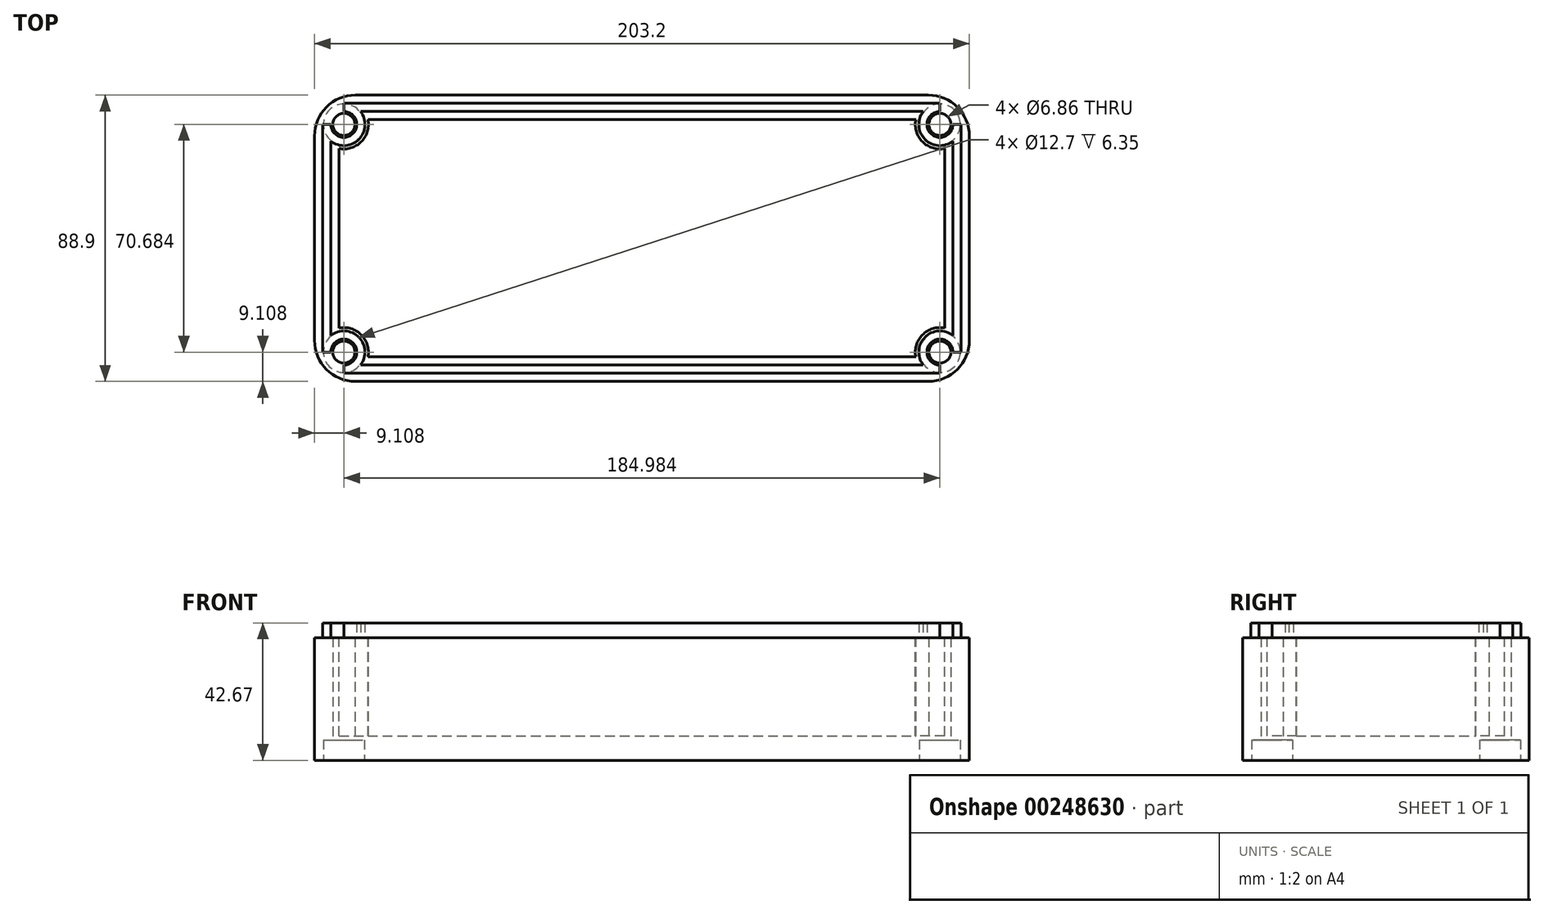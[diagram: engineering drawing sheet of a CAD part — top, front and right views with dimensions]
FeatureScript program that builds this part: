
annotation { "Feature Type Name" : "Feature", "Feature Type Description" : "" }
export const myFeature = defineFeature(function(context is Context, id is Id, definition is map)
    precondition{}
    {
        {
            var Q0;
            Q0=qCreatedBy(makeId("Top.planeOp"),FACE);
            var sketch = newSketch(context, id + "F0", { "sketchPlane" : qUnion([Q0])});
            skLineSegment(sketch, "E0", {"start": v(12.7, 0) * mm, "end": v(190.5, 0) * mm});
            skArc(sketch, "E1", {"start": v(190.5, 0) * mm, "mid": v(199.48, 3.72) * mm, "end": v(203.2, 12.7) * mm});
            skLineSegment(sketch, "E2", {"start": v(203.2, 12.7) * mm, "end": v(203.2, 44.45) * mm});
            skArc(sketch, "E3", {"start": v(0, 12.7) * mm, "mid": v(3.72, 3.72) * mm, "end": v(12.7, 0) * mm});
            skLineSegment(sketch, "E4", {"start": v(0, 12.7) * mm, "end": v(0, 44.45) * mm});
            skLineSegment(sketch, "E5", {"start": v(0, 44.45) * mm, "end": v(203.2, 44.45) * mm, "construction": true});
            skArc(sketch, "E6.MirrorCS", {"start": v(190.5, 88.9) * mm, "mid": v(199.48, 85.18) * mm, "end": v(203.2, 76.2) * mm});
            skArc(sketch, "E7.MirrorCS", {"start": v(0, 76.2) * mm, "mid": v(3.72, 85.18) * mm, "end": v(12.7, 88.9) * mm});
            skLineSegment(sketch, "E8.MirrorCS", {"start": v(12.7, 88.9) * mm, "end": v(190.5, 88.9) * mm});
            skLineSegment(sketch, "E9.MirrorCS", {"start": v(203.2, 76.2) * mm, "end": v(203.2, 44.45) * mm});
            skLineSegment(sketch, "E10.MirrorCS", {"start": v(0, 76.2) * mm, "end": v(0, 44.45) * mm});
            skSolve(sketch);
        }
        {
            var Q0;
            Q0=makeQuery(id+"F0.imprint","IMPRINT",FACE,{"disambiguationData":[TD([[makeQuery(id+"F0.imprint","IMPRINT",EDGE,{"derivedFrom":sQuery(id+"F0.wireOp",EDGE,"E0")}),1.0]])]});
            extrude(context, id + "F1", {"entities" : qUnion([Q0]), "depth" : 38.1 * mm});
        }
        {
            var Q0;
            Q0=makeQuery(id+"F1.opExtrude","CAP_FACE",FACE,{"disambiguationData":[OSD([sQuery(id+"F0.wireOp",EDGE,"E0"),sQuery(id+"F0.wireOp",EDGE,"E1"),sQuery(id+"F0.wireOp",EDGE,"E2"),sQuery(id+"F0.wireOp",EDGE,"E3"),sQuery(id+"F0.wireOp",EDGE,"E4"),sQuery(id+"F0.wireOp",EDGE,"E6.MirrorCS"),sQuery(id+"F0.wireOp",EDGE,"E7.MirrorCS"),sQuery(id+"F0.wireOp",EDGE,"E8.MirrorCS"),sQuery(id+"F0.wireOp",EDGE,"E9.MirrorCS"),sQuery(id+"F0.wireOp",EDGE,"E10.MirrorCS")])],"isStart":false});
            shell(context, id + "F2", {"entities" : qUnion([Q0]), "thickness" : 7.62 * mm});
        }
        {
            var Q0;
            Q0=makeQuery(id+"F1.opExtrude","CAP_FACE",FACE,{"disambiguationData":[OSD([sQuery(id+"F0.wireOp",EDGE,"E0"),sQuery(id+"F0.wireOp",EDGE,"E1"),sQuery(id+"F0.wireOp",EDGE,"E2"),sQuery(id+"F0.wireOp",EDGE,"E3"),sQuery(id+"F0.wireOp",EDGE,"E4"),sQuery(id+"F0.wireOp",EDGE,"E6.MirrorCS"),sQuery(id+"F0.wireOp",EDGE,"E7.MirrorCS"),sQuery(id+"F0.wireOp",EDGE,"E8.MirrorCS"),sQuery(id+"F0.wireOp",EDGE,"E9.MirrorCS"),sQuery(id+"F0.wireOp",EDGE,"E10.MirrorCS")])],"isStart":false});
            var sketch = newSketch(context, id + "F3", { "sketchPlane" : qUnion([Q0])});
            skCircle(sketch, "E11", {"center": v(9.1, 79.8) * mm, "radius": 7.62 * mm});
            skLineSegment(sketch, "E12", {"start": v(101.6, 81.28) * mm, "end": v(101.6, 7.62) * mm, "construction": true});
            skLineSegment(sketch, "E13", {"start": v(7.62, 44.45) * mm, "end": v(195.58, 44.45) * mm, "construction": true});
            skCircle(sketch, "E14.MirrorC", {"center": v(194.1, 79.8) * mm, "radius": 7.62 * mm});
            skCircle(sketch, "E15.MirrorC", {"center": v(9.1, 9.1) * mm, "radius": 7.62 * mm});
            skCircle(sketch, "E16.MirrorC", {"center": v(194.1, 9.1) * mm, "radius": 7.62 * mm});
            skSolve(sketch);
        }
        {
            var Q0;
            Q0 = qSketchRegion(id + "F3", true);
            var Q1;
            Q1=makeQuery(id+"F2.opShell","OFFSET_FACE",FACE,{"disambiguationData":[OSD([sQuery(id+"F0.wireOp",EDGE,"E0"),sQuery(id+"F0.wireOp",EDGE,"E1"),sQuery(id+"F0.wireOp",EDGE,"E2"),sQuery(id+"F0.wireOp",EDGE,"E3"),sQuery(id+"F0.wireOp",EDGE,"E4"),sQuery(id+"F0.wireOp",EDGE,"E6.MirrorCS"),sQuery(id+"F0.wireOp",EDGE,"E7.MirrorCS"),sQuery(id+"F0.wireOp",EDGE,"E8.MirrorCS"),sQuery(id+"F0.wireOp",EDGE,"E9.MirrorCS"),sQuery(id+"F0.wireOp",EDGE,"E10.MirrorCS")])]});
            extrude(context, id + "F4", {"entities" : qUnion([Q0]), "operationType" : NewBodyOperationType.ADD, "endBound" : BoundingType.UP_TO_SURFACE, "oppositeDirection" : true, "endBoundEntityFace" : qUnion([Q1]), "depth" : 25.4 * mm});
        }
        {
            var Q0;
            Q0=makeQuery(id+"F4.boolean.opBoolean","MERGE",FACE,{"derivedFrom":[makeQuery(id+"F1.opExtrude","CAP_FACE",FACE,{"disambiguationData":[OSD([sQuery(id+"F0.wireOp",EDGE,"E0"),sQuery(id+"F0.wireOp",EDGE,"E1"),sQuery(id+"F0.wireOp",EDGE,"E2"),sQuery(id+"F0.wireOp",EDGE,"E3"),sQuery(id+"F0.wireOp",EDGE,"E4"),sQuery(id+"F0.wireOp",EDGE,"E6.MirrorCS"),sQuery(id+"F0.wireOp",EDGE,"E7.MirrorCS"),sQuery(id+"F0.wireOp",EDGE,"E8.MirrorCS"),sQuery(id+"F0.wireOp",EDGE,"E9.MirrorCS"),sQuery(id+"F0.wireOp",EDGE,"E10.MirrorCS")])],"isStart":false}),makeQuery(id+"F4.opExtrude","CAP_FACE",FACE,{"disambiguationData":[OSD([sQuery(id+"F3.wireOp",EDGE,"E14.MirrorC")])],"isStart":true}),makeQuery(id+"F4.opExtrude","CAP_FACE",FACE,{"disambiguationData":[OSD([sQuery(id+"F3.wireOp",EDGE,"E11")])],"isStart":true}),makeQuery(id+"F4.opExtrude","CAP_FACE",FACE,{"disambiguationData":[OSD([sQuery(id+"F3.wireOp",EDGE,"E15.MirrorC")])],"isStart":true}),makeQuery(id+"F4.opExtrude","CAP_FACE",FACE,{"disambiguationData":[OSD([sQuery(id+"F3.wireOp",EDGE,"E16.MirrorC")])],"isStart":true})]});
            var sketch = newSketch(context, id + "F5", { "sketchPlane" : qUnion([Q0])});
            skLineSegment(sketch, "E17.0", {"start": v(101.6, 86.36) * mm, "end": v(194.1, 86.36) * mm});
            skLineSegment(sketch, "E18.0", {"start": v(200.66, 44.45) * mm, "end": v(200.66, 79.8) * mm});
            skLineSegment(sketch, "E19", {"start": v(7.62, 44.45) * mm, "end": v(195.58, 44.45) * mm, "construction": true});
            skLineSegment(sketch, "E20", {"start": v(101.6, 81.28) * mm, "end": v(101.6, 7.62) * mm, "construction": true});
            skLineSegment(sketch, "E21.0", {"start": v(101.6, 83.82) * mm, "end": v(188.9, 83.82) * mm});
            skLineSegment(sketch, "E22.0", {"start": v(198.12, 44.45) * mm, "end": v(198.12, 74.6) * mm});
            skCircle(sketch, "E23", {"center": v(194.1, 79.8) * mm, "radius": 6.57 * mm});
            skCircle(sketch, "E24", {"center": v(194.1, 79.8) * mm, "radius": 4.03 * mm});
            skCircle(sketch, "E25.MirrorC", {"center": v(9.1, 79.8) * mm, "radius": 4.03 * mm});
            skCircle(sketch, "E26.MirrorC", {"center": v(9.1, 79.8) * mm, "radius": 6.57 * mm});
            skLineSegment(sketch, "E27.MirrorCS", {"start": v(5.08, 44.45) * mm, "end": v(5.08, 74.6) * mm});
            skLineSegment(sketch, "E28.MirrorCS", {"start": v(101.6, 83.82) * mm, "end": v(14.3, 83.82) * mm});
            skLineSegment(sketch, "E29.MirrorCS", {"start": v(101.6, 86.36) * mm, "end": v(9.1, 86.36) * mm});
            skLineSegment(sketch, "E30.MirrorCS", {"start": v(2.54, 44.45) * mm, "end": v(2.54, 79.8) * mm});
            skLineSegment(sketch, "E31.MirrorCS", {"start": v(101.6, 5.08) * mm, "end": v(188.9, 5.08) * mm});
            skLineSegment(sketch, "E32.MirrorCS", {"start": v(200.66, 44.45) * mm, "end": v(200.66, 9.1) * mm});
            skLineSegment(sketch, "E33.MirrorCS", {"start": v(101.6, 2.54) * mm, "end": v(194.1, 2.54) * mm});
            skCircle(sketch, "E34.MirrorC", {"center": v(194.1, 9.1) * mm, "radius": 4.03 * mm});
            skCircle(sketch, "E35.MirrorC", {"center": v(194.1, 9.1) * mm, "radius": 6.57 * mm});
            skLineSegment(sketch, "E36.MirrorCS", {"start": v(198.12, 44.45) * mm, "end": v(198.12, 14.3) * mm});
            skCircle(sketch, "E37.MirrorC", {"center": v(9.1, 9.1) * mm, "radius": 4.03 * mm});
            skCircle(sketch, "E38.MirrorC", {"center": v(9.1, 9.1) * mm, "radius": 6.57 * mm});
            skLineSegment(sketch, "E39.MirrorCS", {"start": v(101.6, 5.08) * mm, "end": v(14.3, 5.08) * mm});
            skLineSegment(sketch, "E40.MirrorCS", {"start": v(101.6, 2.54) * mm, "end": v(9.1, 2.54) * mm});
            skLineSegment(sketch, "E41.MirrorCS", {"start": v(5.08, 44.45) * mm, "end": v(5.08, 14.3) * mm});
            skLineSegment(sketch, "E42.MirrorCS", {"start": v(2.54, 44.45) * mm, "end": v(2.54, 9.1) * mm});
            skLineSegment(sketch, "E43", {"start": v(200.66, 79.8) * mm, "end": v(198.12, 79.8) * mm});
            skLineSegment(sketch, "E44", {"start": v(194.1, 86.36) * mm, "end": v(194.1, 83.82) * mm});
            skLineSegment(sketch, "E45.MirrorCS", {"start": v(194.1, 2.54) * mm, "end": v(194.1, 5.08) * mm});
            skLineSegment(sketch, "E46.MirrorCS", {"start": v(200.66, 9.1) * mm, "end": v(198.12, 9.1) * mm});
            skLineSegment(sketch, "E47.MirrorCS", {"start": v(9.1, 86.36) * mm, "end": v(9.1, 83.82) * mm});
            skLineSegment(sketch, "E48.MirrorCS", {"start": v(2.54, 79.8) * mm, "end": v(5.08, 79.8) * mm});
            skLineSegment(sketch, "E49.MirrorCS", {"start": v(2.54, 9.1) * mm, "end": v(5.08, 9.1) * mm});
            skLineSegment(sketch, "E50.MirrorCS", {"start": v(9.1, 2.54) * mm, "end": v(9.1, 5.08) * mm});
            skSolve(sketch);
        }
        {
            var Q0;
            {var subQ4=sQuery(id+"F5.wireOp",EDGE,"E47.MirrorCS");Q0=makeQuery(id+"F5.imprint","IMPRINT",FACE,{"disambiguationData":[TD([[makeQuery(id+"F5.imprint","IMPRINT",EDGE,{"derivedFrom":subQ4}),1.0]])]});}
            var Q1;
            {var subQ5=sQuery(id+"F5.wireOp",EDGE,"E17.0");Q1=makeQuery(id+"F5.imprint","IMPRINT",FACE,{"disambiguationData":[TD([[makeQuery(id+"F5.imprint","IMPRINT",EDGE,{"derivedFrom":subQ5}),-1.0]])]});}
            var Q2;
            {var subQ0=sQuery(id+"F5.wireOp",EDGE,"E43");Q2=makeQuery(id+"F5.imprint","IMPRINT",FACE,{"disambiguationData":[TD([[makeQuery(id+"F5.imprint","IMPRINT",EDGE,{"derivedFrom":subQ0}),1.0]])]});}
            var Q3;
            {var subQ1=sQuery(id+"F5.wireOp",EDGE,"E18.0");Q3=makeQuery(id+"F5.imprint","IMPRINT",FACE,{"disambiguationData":[TD([[makeQuery(id+"F5.imprint","IMPRINT",EDGE,{"derivedFrom":subQ1}),1.0]])]});}
            var Q4;
            {var subQ4=sQuery(id+"F5.wireOp",EDGE,"E45.MirrorCS");Q4=makeQuery(id+"F5.imprint","IMPRINT",FACE,{"disambiguationData":[TD([[makeQuery(id+"F5.imprint","IMPRINT",EDGE,{"derivedFrom":subQ4}),1.0]])]});}
            var Q5;
            {var subQ4=sQuery(id+"F5.wireOp",EDGE,"E31.MirrorCS");Q5=makeQuery(id+"F5.imprint","IMPRINT",FACE,{"disambiguationData":[TD([[makeQuery(id+"F5.imprint","IMPRINT",EDGE,{"derivedFrom":subQ4}),-1.0]])]});}
            var Q6;
            {var subQ2=sQuery(id+"F5.wireOp",EDGE,"E49.MirrorCS");Q6=makeQuery(id+"F5.imprint","IMPRINT",FACE,{"disambiguationData":[TD([[makeQuery(id+"F5.imprint","IMPRINT",EDGE,{"derivedFrom":subQ2}),1.0]])]});}
            var Q7;
            {var subQ4=sQuery(id+"F5.wireOp",EDGE,"E27.MirrorCS");Q7=makeQuery(id+"F5.imprint","IMPRINT",FACE,{"disambiguationData":[TD([[makeQuery(id+"F5.imprint","IMPRINT",EDGE,{"derivedFrom":subQ4}),1.0]])]});}
            extrude(context, id + "F6", {"entities" : qUnion([Q0, Q1, Q2, Q3, Q4, Q5, Q6, Q7]), "operationType" : NewBodyOperationType.ADD, "depth" : 4.57 * mm});
        }
        {
            var Q0;
            Q0=qCreatedBy(makeId("Top.planeOp"),FACE);
            var sketch = newSketch(context, id + "F7", { "sketchPlane" : qUnion([Q0])});
            skPoint(sketch, "E51", {"position": v(9.1, 79.8) * mm});
            skPoint(sketch, "E52", {"position": v(194.1, 79.8) * mm});
            skPoint(sketch, "E53", {"position": v(194.1, 9.1) * mm});
            skPoint(sketch, "E54", {"position": v(9.1, 9.1) * mm});
            skSolve(sketch);
        }
        {
            var Q0;
            Q0=sQuery(id+"F7.wireOp",VERTEX,"E52");
            var Q1;
            Q1=sQuery(id+"F7.wireOp",VERTEX,"E53");
            var Q2;
            Q2=sQuery(id+"F7.wireOp",VERTEX,"E54");
            var Q3;
            Q3=sQuery(id+"F7.wireOp",VERTEX,"E51");
            var Q4;
            Q4=makeQuery(id+"F1.opExtrude","SWEPT_BODY",BODY,{"disambiguationData":[OSD([sQuery(id+"F0.wireOp",EDGE,"E0"),sQuery(id+"F0.wireOp",EDGE,"E1"),sQuery(id+"F0.wireOp",EDGE,"E2"),sQuery(id+"F0.wireOp",EDGE,"E3"),sQuery(id+"F0.wireOp",EDGE,"E4"),sQuery(id+"F0.wireOp",EDGE,"E6.MirrorCS"),sQuery(id+"F0.wireOp",EDGE,"E7.MirrorCS"),sQuery(id+"F0.wireOp",EDGE,"E8.MirrorCS"),sQuery(id+"F0.wireOp",EDGE,"E9.MirrorCS"),sQuery(id+"F0.wireOp",EDGE,"E10.MirrorCS")])]});
            hole(context, id + "F8", {"style" : HoleStyle.C_BORE, "endStyle" : HoleEndStyle.THROUGH, "oppositeDirection" : true, "holeDiameter" : 6.86 * mm, "cBoreDiameter" : 12.7 * mm, "cBoreDepth" : 6.35 * mm, "tappedDepth" : 12.7 * mm, "tapClearance" : 3, "locations" : qUnion([Q0, Q1, Q2, Q3]), "scope" : qUnion([Q4])});
        }
    });
